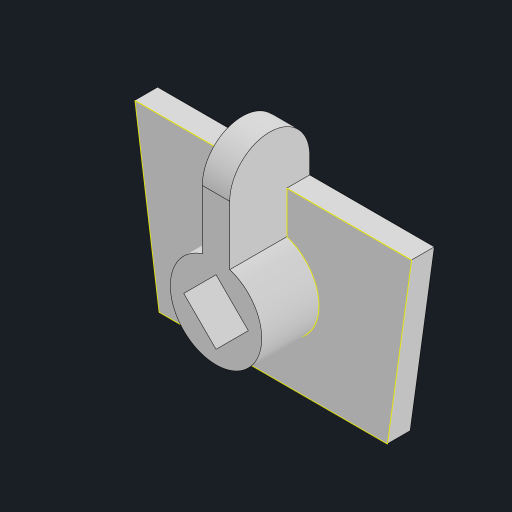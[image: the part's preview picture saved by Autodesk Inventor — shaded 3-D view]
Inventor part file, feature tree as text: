
AUTODESK INVENTOR PART (.ipt)
format: ipt  version: 2023 (Build 270158000, 158)  size: 152,064 bytes
history: native  units: mm
features: sketch x5, extrude x4, other x1
ambient origin geometry x8: Origin, YZ Plane, XZ Plane, XY Plane, X Axis, Y Axis, Z Axis, Center Point
bodies: Body1 (feature_tree)
feature tree (10):
  other  "ソリッド1"
  extrude  "押し出し1"  Depth=2.0mm TaperAngle=0.0deg
  extrude  "押し出し3"  Depth=24.229759mm
  extrude  "押し出し4"  Depth=20.0mm
  extrude  "押し出し5"  Depth=15.0mm
  sketch  "スケッチ7"
  sketch  "スケッチ1"
  sketch  "スケッチ3"
  sketch  "スケッチ4"
  sketch  "スケッチ5"
